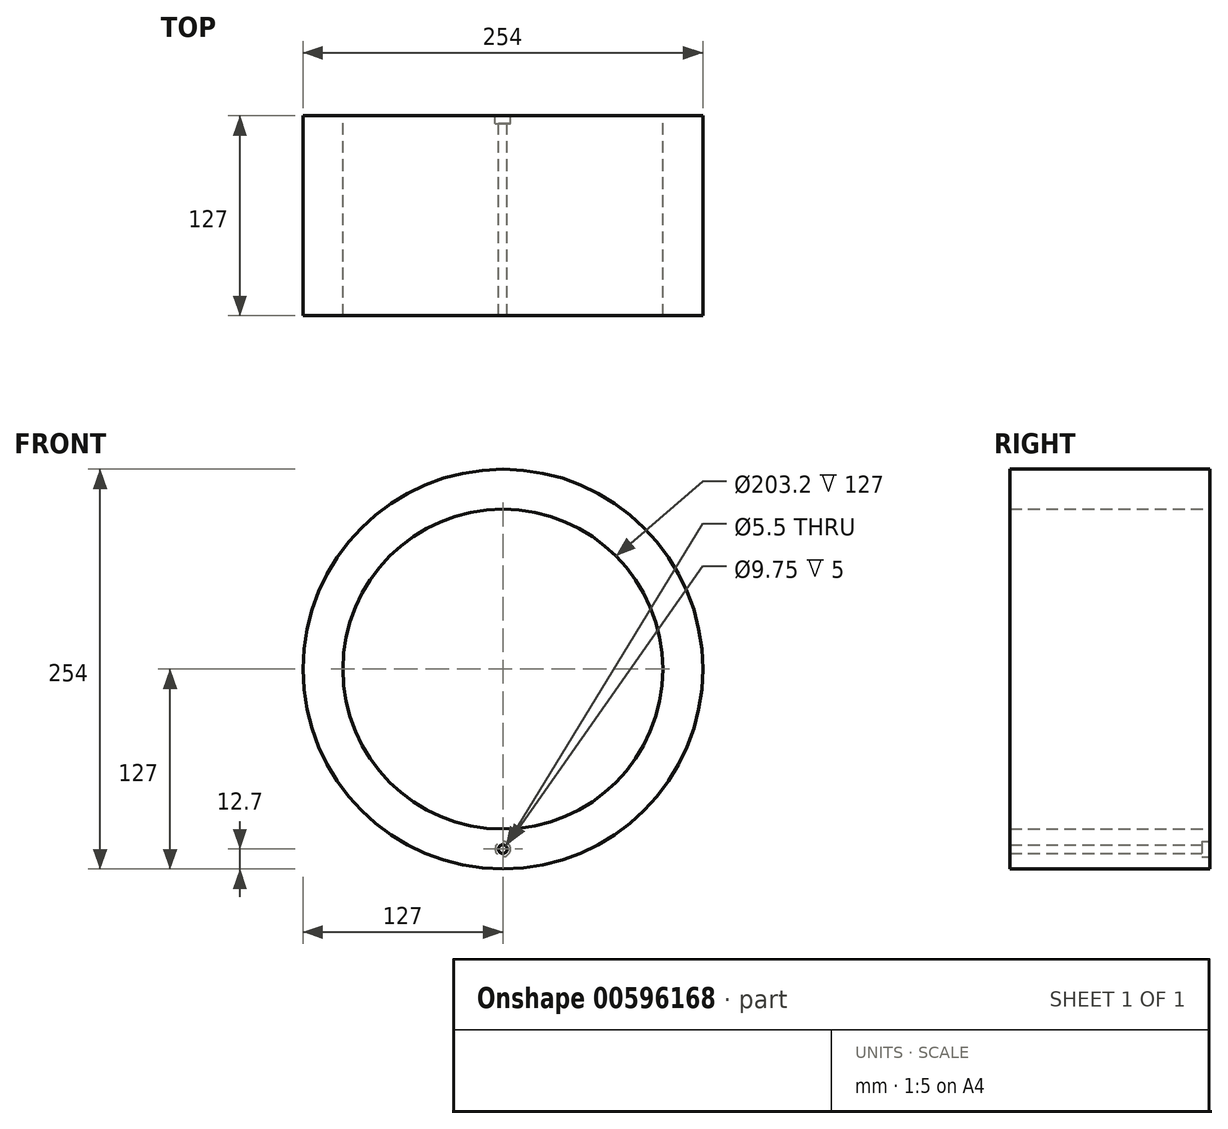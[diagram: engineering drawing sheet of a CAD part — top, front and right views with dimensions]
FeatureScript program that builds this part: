
annotation { "Feature Type Name" : "Feature", "Feature Type Description" : "" }
export const myFeature = defineFeature(function(context is Context, id is Id, definition is map)
    precondition{}
    {
        {
            var Q0;
            Q0=qCreatedBy(makeId("Front.planeOp"),FACE);
            var sketch = newSketch(context, id + "F0", { "sketchPlane" : qUnion([Q0])});
            skCircle(sketch, "E0", {"center": v(0, 0) * mm, "radius": 101.6 * mm});
            skCircle(sketch, "E1", {"center": v(0, 0) * mm, "radius": 127 * mm});
            skSolve(sketch);
        }
        {
            var Q0;
            Q0 = qSketchRegion(id + "F0", true);
            extrude(context, id + "F1", {"entities" : qUnion([Q0]), "depth" : 127 * mm, "offsetDistance" : 25.4 * mm});
        }
        {
            var Q0;
            Q0=makeQuery(id+"F1.opExtrude","CAP_FACE",FACE,{"disambiguationData":[OSD([sQuery(id+"F0.wireOp",EDGE,"E0"),sQuery(id+"F0.wireOp",EDGE,"E1")])],"isStart":true});
            var sketch = newSketch(context, id + "F2", { "sketchPlane" : qUnion([Q0])});
            skLineSegment(sketch, "E2", {"start": v(0, 0) * mm, "end": v(0, -114.3) * mm});
            skSolve(sketch);
        }
        {
            var Q0;
            Q0=sQuery(id+"F2.wireOp",VERTEX,"E2.start");
            var Q1;
            Q1=sQuery(id+"F2.wireOp",VERTEX,"E2.end");
            var Q2;
            Q2=makeQuery(id+"F1.opExtrude","SWEPT_BODY",BODY,{"disambiguationData":[OSD([sQuery(id+"F0.wireOp",EDGE,"E0"),sQuery(id+"F0.wireOp",EDGE,"E1")])]});
            hole(context, id + "F3", {"style" : HoleStyle.C_BORE, "endStyle" : HoleEndStyle.THROUGH, "standardTappedOrClearance" : lookupTablePath({ "standard" : "ISO", "fit" : "Normal", "size" : "M5", "type" : "Clearance" }), "standardBlindInLast" : lookupTablePath({ "fit" : "Standard", "standard" : "ISO", "size" : "M5", "type" : "Clearance" }), "holeDiameter" : 5.5 * mm, "cBoreDiameter" : 9.75 * mm, "cBoreDepth" : 5 * mm, "majorDiameter" : 6.35 * mm, "isTappedThrough" : true, "tappedDepth" : 12.7 * mm, "tapClearance" : 3, "locations" : qUnion([Q0, Q1]), "scope" : qUnion([Q2])});
        }
    });
